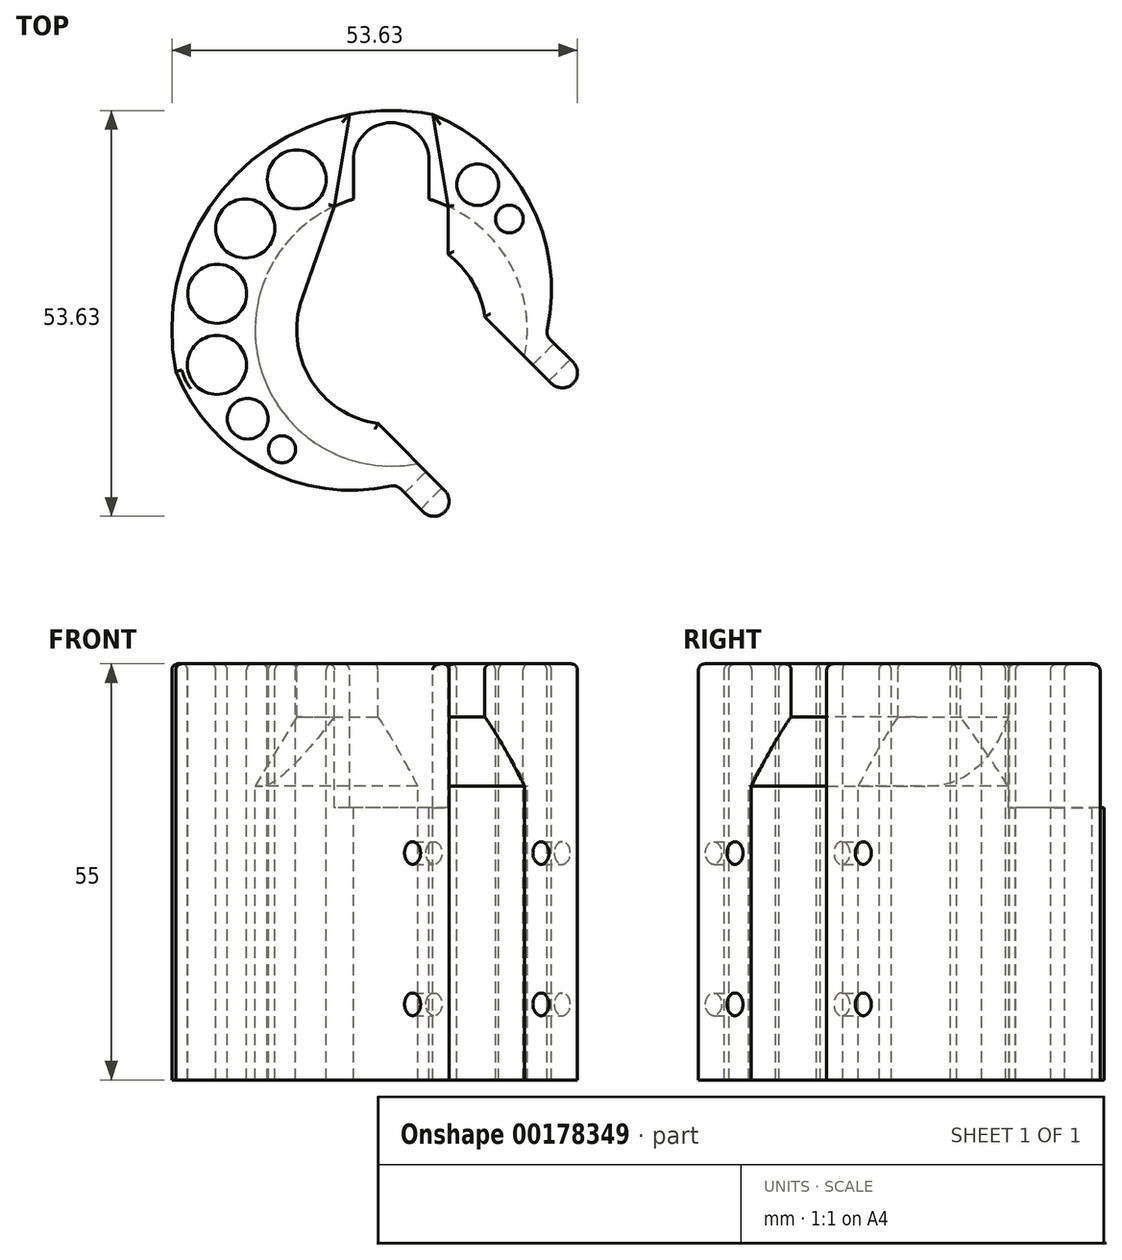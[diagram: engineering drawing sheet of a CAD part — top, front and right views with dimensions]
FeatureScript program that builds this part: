
annotation { "Feature Type Name" : "Feature", "Feature Type Description" : "" }
export const myFeature = defineFeature(function(context is Context, id is Id, definition is map)
    precondition{}
    {
        {
            var Q0;
            Q0=qCreatedBy(makeId("Front.planeOp"),FACE);
            var sketch = newSketch(context, id + "F0", { "sketchPlane" : qUnion([Q0])});
            skLineSegment(sketch, "E0.bottom", {"start": v(-18, 27.5) * mm, "end": v(-29, 27.5) * mm});
            skLineSegment(sketch, "E0.top", {"start": v(-18, -27.5) * mm, "end": v(-29, -27.5) * mm});
            skLineSegment(sketch, "E0.left", {"start": v(-18, 27.5) * mm, "end": v(-18, -27.5) * mm});
            skLineSegment(sketch, "E0.right", {"start": v(-29, 27.5) * mm, "end": v(-29, -27.5) * mm});
            skPoint(sketch, "E1", {"position": v(-18, 0) * mm});
            skLineSegment(sketch, "E2", {"start": v(0, 26.11) * mm, "end": v(0, -24.38) * mm, "construction": true});
            skSolve(sketch);
        }
        {
            var Q0;
            Q0=makeQuery(id+"F0.imprint","IMPRINT",FACE,{"disambiguationData":[TD([[makeQuery(id+"F0.imprint","IMPRINT",EDGE,{"derivedFrom":sQuery(id+"F0.wireOp",EDGE,"E0.bottom")}),1.0]])]});
            var Q1;
            Q1=sQuery(id+"F0.wireOp",EDGE,"E2");
            revolve(context, id + "F1", {"entities" : qUnion([Q0]), "axis" : qUnion([Q1]), "revolveType" : RevolveType.FULL});
        }
        {
            var Q0;
            Q0=makeQuery(id+"F1.opRevolve","SWEPT_FACE",FACE,{"disambiguationData":[OSD([sQuery(id+"F0.wireOp",EDGE,"E0.bottom")])]});
            var sketch = newSketch(context, id + "F2", { "sketchPlane" : qUnion([Q0])});
            skCircle(sketch, "E3", {"center": v(0, 22.4) * mm, "radius": 5 * mm});
            skLineSegment(sketch, "E4", {"start": v(5, 22.4) * mm, "end": v(5, 17.3) * mm});
            skLineSegment(sketch, "E5", {"start": v(-5, 22.4) * mm, "end": v(-5, 17.3) * mm});
            skLineSegment(sketch, "E6", {"start": v(-5.5, 28.47) * mm, "end": v(5.5, 28.47) * mm});
            skLineSegment(sketch, "E7", {"start": v(-7.5, 16.36) * mm, "end": v(7.5, 16.36) * mm});
            skLineSegment(sketch, "E8", {"start": v(-5.5, 28.47) * mm, "end": v(-7.5, 16.36) * mm});
            skLineSegment(sketch, "E9", {"start": v(5.5, 28.47) * mm, "end": v(7.5, 16.36) * mm});
            skLineSegment(sketch, "E10.bottom", {"start": v(3.51, -17.65) * mm, "end": v(-6.98, -28.15) * mm});
            skLineSegment(sketch, "E10.top", {"start": v(8.49, -22.63) * mm, "end": v(-2, -33.12) * mm});
            skLineSegment(sketch, "E10.left", {"start": v(3.51, -17.65) * mm, "end": v(8.49, -22.63) * mm});
            skLineSegment(sketch, "E10.right", {"start": v(-6.98, -28.15) * mm, "end": v(-2, -33.12) * mm});
            skLineSegment(sketch, "E11.bottom", {"start": v(17.65, -3.51) * mm, "end": v(28.15, 6.98) * mm});
            skLineSegment(sketch, "E11.top", {"start": v(22.63, -8.49) * mm, "end": v(33.12, 2) * mm});
            skLineSegment(sketch, "E11.left", {"start": v(17.65, -3.51) * mm, "end": v(22.63, -8.49) * mm});
            skLineSegment(sketch, "E11.right", {"start": v(28.15, 6.98) * mm, "end": v(33.12, 2) * mm});
            skLineSegment(sketch, "E12", {"start": v(20.48, -0.68) * mm, "end": v(25.46, -5.66) * mm});
            skLineSegment(sketch, "E13", {"start": v(0.68, -20.48) * mm, "end": v(5.66, -25.46) * mm});
            skLineSegment(sketch, "E14", {"start": v(0, 10.06) * mm, "end": v(0, 36.25) * mm, "construction": true});
            skLineSegment(sketch, "E15", {"start": v(0, 0) * mm, "end": v(32.33, -32.33) * mm, "construction": true});
            skLineSegment(sketch, "E16", {"start": v(0, 0) * mm, "end": v(-47.08, 0) * mm, "construction": true});
            skPoint(sketch, "E17", {"position": v(0, 29) * mm});
            skLineSegment(sketch, "E18", {"start": v(-28.47, 5.5) * mm, "end": v(-28.47, -5.5) * mm});
            skArc(sketch, "E19", {"start": v(20.48, -0.68) * mm, "mid": v(18.44, 16.7) * mm, "end": v(5.5, 28.47) * mm});
            skArc(sketch, "E20", {"start": v(-28.47, -5.5) * mm, "mid": v(-16.7, -18.44) * mm, "end": v(0.68, -20.48) * mm});
            skLineSegment(sketch, "E21", {"start": v(0, 0) * mm, "end": v(-29.09, 29.09) * mm, "construction": true});
            skCircle(sketch, "E22", {"center": v(-19.3, 13.42) * mm, "radius": 3.9 * mm});
            skCircle(sketch, "E23", {"center": v(0, 0) * mm, "radius": 23.5 * mm, "construction": true});
            skCircle(sketch, "E24", {"center": v(-23, 4.78) * mm, "radius": 3.9 * mm});
            skCircle(sketch, "E25", {"center": v(-23.04, -4.62) * mm, "radius": 3.9 * mm});
            skCircle(sketch, "E26", {"center": v(11.44, 19.2) * mm, "radius": 2.75 * mm});
            skCircle(sketch, "E27", {"center": v(-12.49, 19.9) * mm, "radius": 3.9 * mm});
            skCircle(sketch, "E28", {"center": v(-18.96, -11.73) * mm, "radius": 2.7 * mm});
            skCircle(sketch, "E29", {"center": v(-14.43, -15.78) * mm, "radius": 1.78 * mm});
            skCircle(sketch, "E30", {"center": v(15.63, 14.66) * mm, "radius": 1.82 * mm});
            skCircle(sketch, "E31", {"center": v(0, 0) * mm, "radius": 12.5 * mm});
            skLineSegment(sketch, "E32", {"start": v(-7.5, 16.36) * mm, "end": v(-11.8, 4.14) * mm});
            skLineSegment(sketch, "E33", {"start": v(7.5, 16.36) * mm, "end": v(7.5, 10) * mm});
            skLineSegment(sketch, "E34", {"start": v(3.51, -17.65) * mm, "end": v(-1.77, -12.37) * mm});
            skLineSegment(sketch, "E35", {"start": v(17.65, -3.51) * mm, "end": v(12.37, 1.77) * mm});
            skSolve(sketch);
        }
        {
            var Q0;
            {var subQ1=sQuery(id+"F2.wireOp",EDGE,"E32");Q0=makeQuery(id+"F2.imprint","IMPRINT",FACE,{"disambiguationData":[TD([[makeQuery(id+"F2.imprint","IMPRINT",EDGE,{"derivedFrom":subQ1}),-1.0]])]});}
            var Q1;
            {var subQ0=sQuery(id+"F2.wireOp",EDGE,"E33");Q1=makeQuery(id+"F2.imprint","IMPRINT",FACE,{"disambiguationData":[TD([[makeQuery(id+"F2.imprint","IMPRINT",EDGE,{"derivedFrom":subQ0}),1.0]])]});}
            extrude(context, id + "F3", {"entities" : qUnion([Q0, Q1]), "operationType" : NewBodyOperationType.ADD, "oppositeDirection" : true, "depth" : 17 * mm, "offsetDistance" : 25 * mm});
        }
        {
            var Q0;
            {var subQ1=sQuery(id+"F2.wireOp",EDGE,"E4");Q0=makeQuery(id+"F2.imprint","IMPRINT",FACE,{"disambiguationData":[TD([[makeQuery(id+"F2.imprint","IMPRINT",EDGE,{"derivedFrom":subQ1}),1.0]])]});}
            var Q1;
            {var subQ0=sQuery(id+"F2.wireOp",EDGE,"E6");Q1=makeQuery(id+"F2.imprint","IMPRINT",FACE,{"disambiguationData":[TD([[makeQuery(id+"F2.imprint","IMPRINT",EDGE,{"derivedFrom":subQ0}),1.0]])]});}
            var Q2;
            {var subQ0=sQuery(id+"F2.wireOp",EDGE,"E5");Q2=makeQuery(id+"F2.imprint","IMPRINT",FACE,{"disambiguationData":[TD([[makeQuery(id+"F2.imprint","IMPRINT",EDGE,{"derivedFrom":subQ0}),1.0]])]});}
            var Q3;
            {var subQ0=sQuery(id+"F2.wireOp",EDGE,"E3");var subQ1=makeQuery(id+"F2.imprint","INTERSECT",VERTEX,{"derivedFrom":[subQ0,sQuery(id+"F2.wireOp",EDGE,"E4")]});Q3=makeQuery(id+"F2.imprint","IMPRINT",FACE,{"disambiguationData":[TD([[makeQuery(id+"F2.imprint","IMPRINT",EDGE,{"disambiguationData":[TD([[subQ1,-1.0]])],"derivedFrom":subQ0}),1.0]])]});}
            var Q4;
            {var subQ0=sQuery(id+"F2.wireOp",EDGE,"E4");Q4=makeQuery(id+"F2.imprint","IMPRINT",FACE,{"disambiguationData":[TD([[makeQuery(id+"F2.imprint","IMPRINT",EDGE,{"derivedFrom":subQ0}),-1.0]])]});}
            extrude(context, id + "F4", {"entities" : qUnion([Q0, Q1, Q2, Q3, Q4]), "operationType" : NewBodyOperationType.REMOVE, "oppositeDirection" : true, "depth" : 19 * mm, "offsetDistance" : 25 * mm});
        }
        {
            var Q0;
            {var subQ0=sQuery(id+"F2.wireOp",EDGE,"E10.top");Q0=makeQuery(id+"F2.imprint","IMPRINT",FACE,{"disambiguationData":[TD([[makeQuery(id+"F2.imprint","IMPRINT",EDGE,{"derivedFrom":subQ0}),-1.0]])]});}
            var Q1;
            {var subQ0=sQuery(id+"F2.wireOp",EDGE,"E11.top");Q1=makeQuery(id+"F2.imprint","IMPRINT",FACE,{"disambiguationData":[TD([[makeQuery(id+"F2.imprint","IMPRINT",EDGE,{"derivedFrom":subQ0}),1.0]])]});}
            var Q2;
            Q2=makeQuery(id+"F1.opRevolve","SWEPT_FACE",FACE,{"disambiguationData":[OSD([sQuery(id+"F0.wireOp",EDGE,"E0.top")])]});
            extrude(context, id + "F5", {"entities" : qUnion([Q0, Q1]), "operationType" : NewBodyOperationType.ADD, "endBound" : BoundingType.UP_TO_SURFACE, "oppositeDirection" : true, "endBoundEntityFace" : qUnion([Q2]), "depth" : 25 * mm});
        }
        {
            var Q0;
            Q0=makeQuery(id+"F5.opExtrude","SWEPT_FACE",FACE,{"disambiguationData":[OSD([sQuery(id+"F2.wireOp",EDGE,"E11.right")])]});
            var sketch = newSketch(context, id + "F6", { "sketchPlane" : qUnion([Q0])});
            skCircle(sketch, "E36", {"center": v(-18, 2.5) * mm, "radius": 1.5 * mm});
            skCircle(sketch, "E37", {"center": v(-18, -17.5) * mm, "radius": 1.5 * mm});
            skSolve(sketch);
        }
        {
            var Q0;
            Q0=makeQuery(id+"F2.imprint","IMPRINT",FACE,{"disambiguationData":[TD([[makeQuery(id+"F2.imprint","IMPRINT",EDGE,{"derivedFrom":sQuery(id+"F2.wireOp",EDGE,"E22")}),1.0]])]});
            var Q1;
            Q1=makeQuery(id+"F2.imprint","IMPRINT",FACE,{"disambiguationData":[TD([[makeQuery(id+"F2.imprint","IMPRINT",EDGE,{"derivedFrom":sQuery(id+"F2.wireOp",EDGE,"E27")}),1.0]])]});
            var Q2;
            {var subQ0=sQuery(id+"F2.wireOp",EDGE,"E3");var subQ1=makeQuery(id+"F2.imprint","INTERSECT",VERTEX,{"derivedFrom":[subQ0,sQuery(id+"F2.wireOp",EDGE,"E4")]});Q2=makeQuery(id+"F2.imprint","IMPRINT",FACE,{"disambiguationData":[TD([[makeQuery(id+"F2.imprint","IMPRINT",EDGE,{"disambiguationData":[TD([[subQ1,-1.0]])],"derivedFrom":subQ0}),1.0]])]});}
            var Q3;
            {var subQ0=sQuery(id+"F2.wireOp",EDGE,"E4");Q3=makeQuery(id+"F2.imprint","IMPRINT",FACE,{"disambiguationData":[TD([[makeQuery(id+"F2.imprint","IMPRINT",EDGE,{"derivedFrom":subQ0}),-1.0]])]});}
            var Q4;
            {var subQ0=sQuery(id+"F2.wireOp",EDGE,"E5");Q4=makeQuery(id+"F2.imprint","IMPRINT",FACE,{"disambiguationData":[TD([[makeQuery(id+"F2.imprint","IMPRINT",EDGE,{"derivedFrom":subQ0}),1.0]])]});}
            var Q5;
            Q5=makeQuery(id+"F2.imprint","IMPRINT",FACE,{"disambiguationData":[TD([[makeQuery(id+"F2.imprint","IMPRINT",EDGE,{"derivedFrom":sQuery(id+"F2.wireOp",EDGE,"E26")}),1.0]])]});
            var Q6;
            Q6=makeQuery(id+"F2.imprint","IMPRINT",FACE,{"disambiguationData":[TD([[makeQuery(id+"F2.imprint","IMPRINT",EDGE,{"derivedFrom":sQuery(id+"F2.wireOp",EDGE,"E30")}),1.0]])]});
            var Q7;
            Q7=makeQuery(id+"F2.imprint","IMPRINT",FACE,{"disambiguationData":[TD([[makeQuery(id+"F2.imprint","IMPRINT",EDGE,{"derivedFrom":sQuery(id+"F2.wireOp",EDGE,"E29")}),1.0]])]});
            var Q8;
            Q8=makeQuery(id+"F2.imprint","IMPRINT",FACE,{"disambiguationData":[TD([[makeQuery(id+"F2.imprint","IMPRINT",EDGE,{"derivedFrom":sQuery(id+"F2.wireOp",EDGE,"E28")}),1.0]])]});
            var Q9;
            Q9=makeQuery(id+"F2.imprint","IMPRINT",FACE,{"disambiguationData":[TD([[makeQuery(id+"F2.imprint","IMPRINT",EDGE,{"derivedFrom":sQuery(id+"F2.wireOp",EDGE,"E25")}),1.0]])]});
            var Q10;
            Q10=makeQuery(id+"F2.imprint","IMPRINT",FACE,{"disambiguationData":[TD([[makeQuery(id+"F2.imprint","IMPRINT",EDGE,{"derivedFrom":sQuery(id+"F2.wireOp",EDGE,"E24")}),1.0]])]});
            var Q11;
            {var subQ3=sQuery(id+"F2.wireOp",EDGE,"E20");Q11=makeQuery(id+"F2.imprint","IMPRINT",FACE,{"disambiguationData":[TD([[makeQuery(id+"F2.imprint","IMPRINT",EDGE,{"derivedFrom":subQ3}),-1.0]])]});}
            var Q12;
            {var subQ3=sQuery(id+"F2.wireOp",EDGE,"E13");Q12=makeQuery(id+"F2.imprint","IMPRINT",FACE,{"disambiguationData":[TD([[makeQuery(id+"F2.imprint","IMPRINT",EDGE,{"derivedFrom":subQ3}),-1.0]])]});}
            var Q13;
            {var subQ0=sQuery(id+"F2.wireOp",EDGE,"E10.right");Q13=makeQuery(id+"F2.imprint","IMPRINT",FACE,{"disambiguationData":[TD([[makeQuery(id+"F2.imprint","IMPRINT",EDGE,{"derivedFrom":subQ0}),1.0]])]});}
            var Q14;
            {var subQ3=sQuery(id+"F2.wireOp",EDGE,"E10.left");Q14=makeQuery(id+"F2.imprint","IMPRINT",FACE,{"disambiguationData":[TD([[makeQuery(id+"F2.imprint","IMPRINT",EDGE,{"derivedFrom":subQ3}),1.0]])]});}
            var Q15;
            {var subQ0=sQuery(id+"F2.wireOp",EDGE,"E11.right");Q15=makeQuery(id+"F2.imprint","IMPRINT",FACE,{"disambiguationData":[TD([[makeQuery(id+"F2.imprint","IMPRINT",EDGE,{"derivedFrom":subQ0}),-1.0]])]});}
            var Q16;
            {var subQ3=sQuery(id+"F2.wireOp",EDGE,"E19");Q16=makeQuery(id+"F2.imprint","IMPRINT",FACE,{"disambiguationData":[TD([[makeQuery(id+"F2.imprint","IMPRINT",EDGE,{"derivedFrom":subQ3}),-1.0]])]});}
            var Q17;
            {var subQ3=sQuery(id+"F2.wireOp",EDGE,"E12");Q17=makeQuery(id+"F2.imprint","IMPRINT",FACE,{"disambiguationData":[TD([[makeQuery(id+"F2.imprint","IMPRINT",EDGE,{"derivedFrom":subQ3}),1.0]])]});}
            extrude(context, id + "F7", {"entities" : qUnion([Q0, Q1, Q2, Q3, Q4, Q5, Q6, Q7, Q8, Q9, Q10, Q11, Q12, Q13, Q14, Q15, Q16, Q17]), "operationType" : NewBodyOperationType.REMOVE, "endBound" : BoundingType.THROUGH_ALL, "oppositeDirection" : true, "depth" : 25 * mm, "offsetDistance" : 25 * mm});
        }
        {
            var Q0;
            Q0=makeQuery(id+"F5.opExtrude","SWEPT_EDGE",EDGE,{"disambiguationData":[OSD([sQuery(id+"F2.wireOp",EDGE,"E10.top"),sQuery(id+"F2.wireOp",EDGE,"E10.right")])]});
            var Q1;
            Q1=makeQuery(id+"F5.opExtrude","SWEPT_EDGE",EDGE,{"disambiguationData":[OSD([sQuery(id+"F2.wireOp",EDGE,"E11.top"),sQuery(id+"F2.wireOp",EDGE,"E11.right")])]});
            var Q2;
            Q2=makeQuery(id+"F7.boolean.opBoolean","COPY",EDGE,{"derivedFrom":makeQuery(id+"F7.opExtrude","SWEPT_EDGE",EDGE,{"disambiguationData":[OSD([sQuery(id+"F0.wireOp",EDGE,"E0.bottom"),sQuery(id+"F0.wireOp",EDGE,"E0.left"),sQuery(id+"F2.wireOp",EDGE,"E10.bottom"),sQuery(id+"F2.wireOp",EDGE,"E10.left")])]})});
            var Q3;
            Q3=makeQuery(id+"F7.boolean.opBoolean","COPY",EDGE,{"derivedFrom":makeQuery(id+"F7.opExtrude","SWEPT_EDGE",EDGE,{"disambiguationData":[OSD([sQuery(id+"F0.wireOp",EDGE,"E0.bottom"),sQuery(id+"F0.wireOp",EDGE,"E0.left"),sQuery(id+"F2.wireOp",EDGE,"E4")])]})});
            var Q4;
            Q4=makeQuery(id+"F4.boolean.opBoolean","COPY",EDGE,{"derivedFrom":makeQuery(id+"F4.opExtrude","SWEPT_EDGE",EDGE,{"disambiguationData":[OSD([sQuery(id+"F0.wireOp",EDGE,"E0.bottom"),sQuery(id+"F0.wireOp",EDGE,"E0.left"),sQuery(id+"F2.wireOp",EDGE,"E7"),sQuery(id+"F2.wireOp",EDGE,"E9")])]})});
            var Q5;
            Q5=makeQuery(id+"F4.boolean.opBoolean","COPY",EDGE,{"derivedFrom":makeQuery(id+"F4.opExtrude","SWEPT_EDGE",EDGE,{"disambiguationData":[OSD([sQuery(id+"F0.wireOp",EDGE,"E0.bottom"),sQuery(id+"F0.wireOp",EDGE,"E0.left"),sQuery(id+"F2.wireOp",EDGE,"E7"),sQuery(id+"F2.wireOp",EDGE,"E8")])]})});
            var Q6;
            Q6=makeQuery(id+"F7.boolean.opBoolean","COPY",EDGE,{"derivedFrom":makeQuery(id+"F7.opExtrude","SWEPT_EDGE",EDGE,{"disambiguationData":[OSD([sQuery(id+"F0.wireOp",EDGE,"E0.bottom"),sQuery(id+"F0.wireOp",EDGE,"E0.left"),sQuery(id+"F2.wireOp",EDGE,"E5")])]})});
            var Q7;
            Q7=makeQuery(id+"F4.boolean.opBoolean","COPY",EDGE,{"derivedFrom":makeQuery(id+"F4.opExtrude","SWEPT_EDGE",EDGE,{"disambiguationData":[OSD([sQuery(id+"F0.wireOp",EDGE,"E0.bottom"),sQuery(id+"F0.wireOp",EDGE,"E0.right"),sQuery(id+"F2.wireOp",EDGE,"E6"),sQuery(id+"F2.wireOp",EDGE,"E9")])]})});
            var Q8;
            Q8=makeQuery(id+"F4.boolean.opBoolean","COPY",EDGE,{"derivedFrom":makeQuery(id+"F4.opExtrude","SWEPT_EDGE",EDGE,{"disambiguationData":[OSD([sQuery(id+"F0.wireOp",EDGE,"E0.bottom"),sQuery(id+"F0.wireOp",EDGE,"E0.right"),sQuery(id+"F2.wireOp",EDGE,"E6"),sQuery(id+"F2.wireOp",EDGE,"E8")])]})});
            var Q9;
            Q9=makeQuery(id+"F7.boolean.opBoolean","COPY",EDGE,{"derivedFrom":makeQuery(id+"F7.opExtrude","SWEPT_EDGE",EDGE,{"disambiguationData":[OSD([sQuery(id+"F2.wireOp",EDGE,"E10.bottom"),sQuery(id+"F2.wireOp",EDGE,"E13"),sQuery(id+"F2.wireOp",EDGE,"f805bfa0-6c3b-483c-aa07-8e93bd6a3935")])]})});
            var Q10;
            Q10=makeQuery(id+"F7.boolean.opBoolean","COPY",EDGE,{"derivedFrom":makeQuery(id+"F7.opExtrude","SWEPT_EDGE",EDGE,{"disambiguationData":[OSD([sQuery(id+"F2.wireOp",EDGE,"E11.bottom"),sQuery(id+"F2.wireOp",EDGE,"E12"),sQuery(id+"F2.wireOp",EDGE,"a9218696-1b7a-4d31-9a07-934ffbfcfd7e")])]})});
            var Q11;
            Q11=makeQuery(id+"F7.boolean.opBoolean","COPY",EDGE,{"derivedFrom":makeQuery(id+"F7.opExtrude","SWEPT_EDGE",EDGE,{"disambiguationData":[OSD([sQuery(id+"F0.wireOp",EDGE,"E0.bottom"),sQuery(id+"F0.wireOp",EDGE,"E0.left"),sQuery(id+"F2.wireOp",EDGE,"E11.bottom"),sQuery(id+"F2.wireOp",EDGE,"E11.left")])]})});
            fillet(context, id + "F8", {"entities" : qUnion([Q0, Q1, Q2, Q3, Q4, Q5, Q6, Q7, Q8, Q9, Q10, Q11]), "radius" : 1.2 * mm, "tangentPropagation" : true, "allowEdgeOverflow" : false});
        }
        {
            var Q0;
            Q0=makeQuery(id+"F7.boolean.opBoolean","COPY",EDGE,{"derivedFrom":makeQuery(id+"F7.opExtrude","SWEPT_EDGE",EDGE,{"disambiguationData":[OSD([sQuery(id+"F2.wireOp",EDGE,"E10.top"),sQuery(id+"F2.wireOp",EDGE,"E13")])]})});
            var Q1;
            Q1=makeQuery(id+"F5.opExtrude","SWEPT_EDGE",EDGE,{"disambiguationData":[OSD([sQuery(id+"F2.wireOp",EDGE,"E10.top"),sQuery(id+"F2.wireOp",EDGE,"E10.left")])]});
            var Q2;
            Q2=makeQuery(id+"F5.opExtrude","SWEPT_EDGE",EDGE,{"disambiguationData":[OSD([sQuery(id+"F2.wireOp",EDGE,"E11.top"),sQuery(id+"F2.wireOp",EDGE,"E11.left")])]});
            var Q3;
            Q3=makeQuery(id+"F7.boolean.opBoolean","COPY",EDGE,{"derivedFrom":makeQuery(id+"F7.opExtrude","SWEPT_EDGE",EDGE,{"disambiguationData":[OSD([sQuery(id+"F2.wireOp",EDGE,"E11.top"),sQuery(id+"F2.wireOp",EDGE,"E12")])]})});
            var Q4;
            Q4=makeQuery(id+"F7.boolean.opBoolean","COPY",EDGE,{"derivedFrom":makeQuery(id+"F7.opExtrude","SWEPT_EDGE",EDGE,{"disambiguationData":[OSD([sQuery(id+"F2.wireOp",EDGE,"E10.top"),sQuery(id+"F2.wireOp",EDGE,"E10.left")])]})});
            var Q5;
            Q5=makeQuery(id+"F7.boolean.opBoolean","COPY",EDGE,{"derivedFrom":makeQuery(id+"F7.opExtrude","SWEPT_EDGE",EDGE,{"disambiguationData":[OSD([sQuery(id+"F2.wireOp",EDGE,"E11.top"),sQuery(id+"F2.wireOp",EDGE,"E11.left")])]})});
            fillet(context, id + "F9", {"entities" : qUnion([Q0, Q1, Q2, Q3, Q4, Q5]), "radius" : 2 * mm, "tangentPropagation" : true, "allowEdgeOverflow" : false});
        }
        {
            var Q0;
            {var subQ0=sQuery(id+"F2.wireOp",EDGE,"E31");Q0=makeQuery(id+"F3.opExtrude","CAP_EDGE",EDGE,{"disambiguationData":[OSD([subQ0]),TDD([makeQuery(id+"F2.imprint","IMPRINT",EDGE,{"disambiguationData":[TD([[makeQuery(id+"F2.imprint","INTERSECT",VERTEX,{"derivedFrom":[subQ0,sQuery(id+"F2.wireOp",EDGE,"E32")]}),-1.0]])],"derivedFrom":subQ0})])],"isStart":false});}
            var Q1;
            {var subQ0=sQuery(id+"F2.wireOp",EDGE,"E31");Q1=makeQuery(id+"F3.opExtrude","CAP_EDGE",EDGE,{"disambiguationData":[OSD([subQ0]),TDD([makeQuery(id+"F2.imprint","IMPRINT",EDGE,{"disambiguationData":[TD([[makeQuery(id+"F2.imprint","INTERSECT",VERTEX,{"derivedFrom":[subQ0,sQuery(id+"F2.wireOp",EDGE,"E33")]}),1.0]])],"derivedFrom":subQ0})])],"isStart":false});}
            chamfer(context, id + "F10", {"entities" : qUnion([Q0, Q1]), "chamferType" : ChamferType.TWO_OFFSETS, "width1" : 6 * mm, "oppositeDirection" : false, "width2" : 10 * mm, "tangentPropagation" : true});
        }
        {
            var Q0;
            {var subQ2=sQuery(id+"F2.wireOp",EDGE,"E10.top");var subQ3=sQuery(id+"F2.wireOp",EDGE,"E32");var subQ4=sQuery(id+"F2.wireOp",EDGE,"E31");var subQ5=sQuery(id+"F2.wireOp",EDGE,"E34");var subQ6=sQuery(id+"F0.wireOp",EDGE,"E0.right");var subQ7=sQuery(id+"F0.wireOp",EDGE,"E0.bottom");var subQ8=sQuery(id+"F0.wireOp",EDGE,"E0.left");Q0=makeQuery(id+"F7.boolean.opBoolean","SPLIT",FACE,{"disambiguationData":[TD([makeQuery(id+"F1.opRevolve","SWEPT_FACE",FACE,{"disambiguationData":[OSD([subQ6])]})])],"derivedFrom":makeQuery(id+"F5.boolean.opBoolean","MERGE",FACE,{"derivedFrom":[makeQuery(id+"F3.boolean.opBoolean","MERGE",FACE,{"derivedFrom":[makeQuery(id+"F1.opRevolve","SWEPT_FACE",FACE,{"disambiguationData":[OSD([subQ7])]}),makeQuery(id+"F3.opExtrude","CAP_FACE",FACE,{"disambiguationData":[OSD([subQ7,subQ8,subQ4,sQuery(id+"F2.wireOp",EDGE,"E33"),sQuery(id+"F2.wireOp",EDGE,"E35")])],"isStart":true}),makeQuery(id+"F3.opExtrude","CAP_FACE",FACE,{"disambiguationData":[OSD([subQ7,subQ8,subQ4,subQ3,subQ5])],"isStart":true})]}),makeQuery(id+"F5.opExtrude","CAP_FACE",FACE,{"disambiguationData":[OSD([subQ7,subQ6,subQ2,sQuery(id+"F2.wireOp",EDGE,"E10.right")])],"isStart":true}),makeQuery(id+"F5.opExtrude","CAP_FACE",FACE,{"disambiguationData":[OSD([subQ7,subQ6,sQuery(id+"F2.wireOp",EDGE,"E11.top"),sQuery(id+"F2.wireOp",EDGE,"E11.right")])],"isStart":true})]})});}
            var Q1;
            {var subQ0=sQuery(id+"F2.wireOp",EDGE,"E35");var subQ2=sQuery(id+"F2.wireOp",EDGE,"E33");var subQ3=sQuery(id+"F2.wireOp",EDGE,"E11.top");var subQ5=sQuery(id+"F2.wireOp",EDGE,"E31");var subQ6=sQuery(id+"F0.wireOp",EDGE,"E0.right");var subQ7=sQuery(id+"F0.wireOp",EDGE,"E0.bottom");var subQ8=sQuery(id+"F0.wireOp",EDGE,"E0.left");Q1=makeQuery(id+"F7.boolean.opBoolean","SPLIT",FACE,{"disambiguationData":[TD([makeQuery(id+"F3.opExtrude","SWEPT_FACE",FACE,{"disambiguationData":[OSD([subQ2])]})])],"derivedFrom":makeQuery(id+"F5.boolean.opBoolean","MERGE",FACE,{"derivedFrom":[makeQuery(id+"F3.boolean.opBoolean","MERGE",FACE,{"derivedFrom":[makeQuery(id+"F1.opRevolve","SWEPT_FACE",FACE,{"disambiguationData":[OSD([subQ7])]}),makeQuery(id+"F3.opExtrude","CAP_FACE",FACE,{"disambiguationData":[OSD([subQ7,subQ8,subQ5,subQ2,subQ0])],"isStart":true}),makeQuery(id+"F3.opExtrude","CAP_FACE",FACE,{"disambiguationData":[OSD([subQ7,subQ8,subQ5,sQuery(id+"F2.wireOp",EDGE,"E32"),sQuery(id+"F2.wireOp",EDGE,"E34")])],"isStart":true})]}),makeQuery(id+"F5.opExtrude","CAP_FACE",FACE,{"disambiguationData":[OSD([subQ7,subQ6,sQuery(id+"F2.wireOp",EDGE,"E10.top"),sQuery(id+"F2.wireOp",EDGE,"E10.right")])],"isStart":true}),makeQuery(id+"F5.opExtrude","CAP_FACE",FACE,{"disambiguationData":[OSD([subQ7,subQ6,subQ3,sQuery(id+"F2.wireOp",EDGE,"E11.right")])],"isStart":true})]})});}
            fillet(context, id + "F11", {"entities" : qUnion([Q0, Q1]), "radius" : 0.8 * mm, "tangentPropagation" : true, "allowEdgeOverflow" : false});
        }
        {
            var Q0;
            Q0=qSketchRegion(id+"F6",true);
            extrude(context, id + "F12", {"entities" : qUnion([Q0]), "operationType" : NewBodyOperationType.REMOVE, "endBound" : BoundingType.THROUGH_ALL, "oppositeDirection" : true, "depth" : 25 * mm});
        }
    });
